# Revit family: UpperCabinet-Vitra-ValarteSeries-62255+62256+62257
name_source: partatom
category: Furniture Systems
revit_build: Autodesk Revit 2017 (Build: 20160225_1515(x64)
units: mm (PartAtom-declared; Revit-internal decimal feet)

## family parameters
Cut with Voids When Loaded = No
Host = Face
OmniClass Number = 23.40.00.00
OmniClass Title = Equipment and Furnishings
Part Type = Normal
Room Calculation Point = No
Round Connector Dimension = Use Diameter
Shared = Yes

## types (3) — shared parameters
BIMobject category = Storage
Construction Type = Wall Mounted
Default Elevation = 1400 mm  [stored 4.59318 ft]
Depth(mm) = 195 mm  [stored 0.639764 ft]
Description = İntegra Upper Cabinet
Design country = Turkey
Height(mm) = 550 mm
IFC Classification = Furniture
Manufacturer = Vitra
Manufacturer name = Vitra
Masterformat 2014 Code = 12 35 30.23
Masterformat 2014 Description = Bathroom Casework
NBS Referans Code = 35-75-08
NBS Referans Description = Bathroom Cabinets
Nominal height = 0.000
Nominal width = 0.000
OmniClass Code = 23-31 25 13
OmniClass Description = Bathroom Cabinets
Product certification = https://vitraglobal.com
Product data url = https://www.vitra.com.tr
Product family = Valarte
Product group = Bathroom Furniture
Technical description = https://www.vitra.com.tr
UNSPSC Code = 30161801
UNSPSC Description = Bathroom Cabinets
URL = https://vitraglobal.com
Uniclass 1.4 Code = L8241
Uniclass 1.4 Description = Bathroom Cabinets
Uniclass 2.0 Code = PR-35-75-08
Uniclass 2.0 Description = Bathroom Cabinets
Uniclass 2015 Code = Pr_40_30_78_03
Uniclass 2015 Name = Bathroom Cabinets
Uniformat II Code = E2010
Uniformat II Description = Fixed Furnishings
Warranty Period (Year) = 2
Weight Net (kg) = 23,000
Width(mm) = 750 mm  [stored 2.46063 ft]
Youtube = https://www.youtube.com

## per-type parameters (varying)
| type | Article No. (default) | Model | Primary Material | Product SKU |
| UpperCabinet-Vitra-ValarteSeries_62255 | 62255 | 62255 | Vitra-MattWhite | 62255 |
| UpperCabinet-Vitra-ValarteSeries_62256 | 62256 | 62256 | Vitra-MattGrey | 62256 |
| UpperCabinet-Vitra-ValarteSeries_62257 | 62257 | 62257 | Vitra-MattIvory | 62257 |

note: [stored X ft] marks values corroborated as IEEE doubles in the binary element streams (Revit-internal decimal feet)

## geometry (parser evidence)
native form markers: Sweep x6
no freeform markers — native parametric forms only
